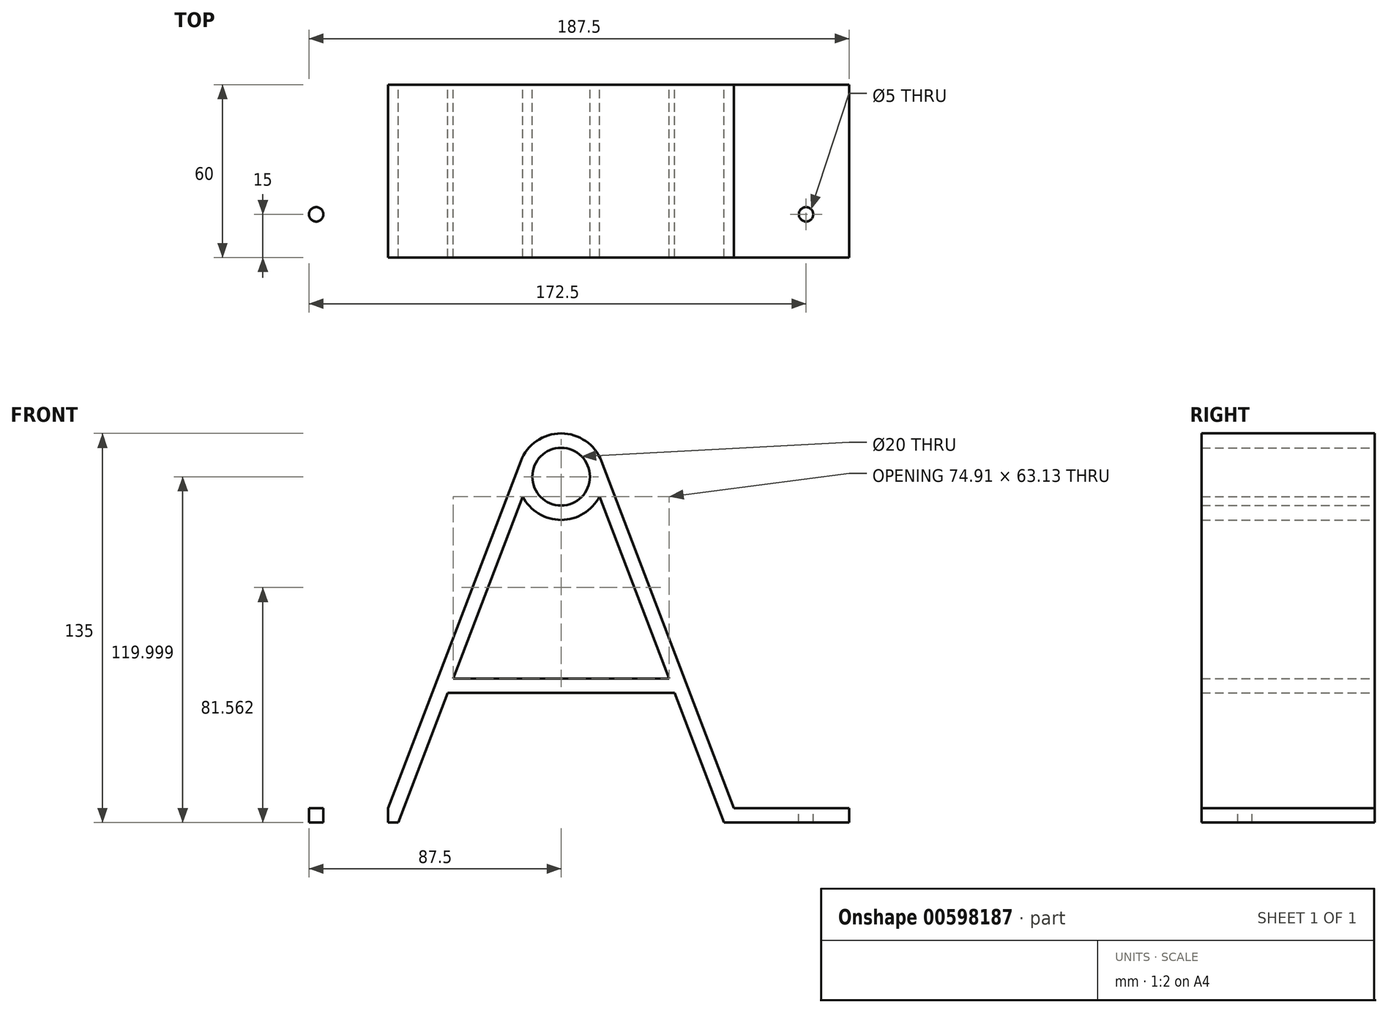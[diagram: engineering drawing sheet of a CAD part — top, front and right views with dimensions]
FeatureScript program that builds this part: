
annotation { "Feature Type Name" : "Feature", "Feature Type Description" : "" }
export const myFeature = defineFeature(function(context is Context, id is Id, definition is map)
    precondition{}
    {
        {
            var Q0;
            Q0=qCreatedBy(makeId("Front.planeOp"),FACE);
            var sketch = newSketch(context, id + "F0", { "sketchPlane" : qUnion([Q0])});
            skLineSegment(sketch, "E0", {"start": v(-100, -81.24) * mm, "end": v(-60, -81.24) * mm});
            skLineSegment(sketch, "E1", {"start": v(-60, -81.24) * mm, "end": v(-14.01, 39.11) * mm});
            skLineSegment(sketch, "E2", {"start": v(0, 109.18) * mm, "end": v(0, -148.57) * mm, "construction": true});
            skLineSegment(sketch, "E3.MirrorCS", {"start": v(60, -81.24) * mm, "end": v(14.01, 39.11) * mm});
            skLineSegment(sketch, "E4.MirrorCS", {"start": v(100, -81.24) * mm, "end": v(60, -81.24) * mm});
            skCircle(sketch, "E5", {"center": v(0, 33.76) * mm, "radius": 15 * mm});
            skCircle(sketch, "E6", {"center": v(0, 33.76) * mm, "radius": 10 * mm});
            skPoint(sketch, "E7.orphan", {"position": v(0, 75.78) * mm});
            skLineSegment(sketch, "E8", {"start": v(-100, -81.24) * mm, "end": v(-100, -86.24) * mm});
            skLineSegment(sketch, "E9", {"start": v(-100, -86.24) * mm, "end": v(100, -86.24) * mm});
            skLineSegment(sketch, "E10", {"start": v(100, -81.24) * mm, "end": v(100, -86.24) * mm});
            skLineSegment(sketch, "E11", {"start": v(-56.56, -86.24) * mm, "end": v(-13.33, 26.88) * mm});
            skLineSegment(sketch, "E12.MirrorCS", {"start": v(56.56, -86.24) * mm, "end": v(13.33, 26.88) * mm});
            skPoint(sketch, "E13.trimOffspring.end.orphan", {"position": v(-5.35, 75.78) * mm});
            skPoint(sketch, "E14.trimOffspring.end.orphan", {"position": v(5.35, 75.78) * mm});
            skPoint(sketch, "E15.orphan", {"position": v(-61.1, -98.12) * mm});
            skPoint(sketch, "E16.orphan", {"position": v(61.1, -98.12) * mm});
            skLineSegment(sketch, "E17", {"start": v(-39.36, -41.24) * mm, "end": v(39.36, -41.24) * mm});
            skLineSegment(sketch, "E18", {"start": v(-37.45, -36.24) * mm, "end": v(37.45, -36.24) * mm});
            skSolve(sketch);
        }
        {
            var Q0;
            Q0=makeQuery(id+"F0.imprint","IMPRINT",FACE,{"disambiguationData":[TD([[makeQuery(id+"F0.imprint","IMPRINT",EDGE,{"derivedFrom":sQuery(id+"F0.wireOp",EDGE,"E0")}),-1.0]])]});
            var Q1;
            {var subQ5=sQuery(id+"F0.wireOp",EDGE,"E3.MirrorCS");Q1=makeQuery(id+"F0.imprint","IMPRINT",FACE,{"disambiguationData":[TD([[makeQuery(id+"F0.imprint","IMPRINT",EDGE,{"derivedFrom":subQ5}),1.0]])]});}
            var Q2;
            Q2=makeQuery(id+"F0.imprint","IMPRINT",FACE,{"disambiguationData":[TD([[makeQuery(id+"F0.imprint","IMPRINT",EDGE,{"derivedFrom":sQuery(id+"F0.wireOp",EDGE,"E6")}),-1.0]])]});
            var Q3;
            {var subQ0=sQuery(id+"F0.wireOp",EDGE,"E17");Q3=makeQuery(id+"F0.imprint","IMPRINT",FACE,{"disambiguationData":[TD([[makeQuery(id+"F0.imprint","IMPRINT",EDGE,{"derivedFrom":subQ0}),1.0]])]});}
            extrude(context, id + "F1", {"entities" : qUnion([Q0, Q1, Q2, Q3]), "endBound" : BoundingType.SYMMETRIC, "depth" : 60 * mm, "offsetDistance" : 25 * mm});
        }
        {
            var Q0;
            Q0=makeQuery(id+"F1.opExtrude","SWEPT_FACE",FACE,{"disambiguationData":[OSD([sQuery(id+"F0.wireOp",EDGE,"E0")])]});
            var sketch = newSketch(context, id + "F2", { "sketchPlane" : qUnion([Q0])});
            skCircle(sketch, "E19", {"center": v(-85, 15) * mm, "radius": 2.5 * mm});
            skCircle(sketch, "E20.MirrorC", {"center": v(-85, -15) * mm, "radius": 2.5 * mm});
            skCircle(sketch, "E21.MirrorC", {"center": v(85, 15) * mm, "radius": 2.5 * mm});
            skCircle(sketch, "E22.MirrorC", {"center": v(85, -15) * mm, "radius": 2.5 * mm});
            skSolve(sketch);
        }
        {
            var Q0;
            Q0=makeQuery(id+"F2.imprint","IMPRINT",FACE,{"disambiguationData":[TD([[makeQuery(id+"F2.imprint","IMPRINT",EDGE,{"derivedFrom":sQuery(id+"F2.wireOp",EDGE,"E19")}),1.0]])]});
            var Q1;
            Q1=makeQuery(id+"F2.imprint","IMPRINT",FACE,{"disambiguationData":[TD([[makeQuery(id+"F2.imprint","IMPRINT",EDGE,{"derivedFrom":sQuery(id+"F2.wireOp",EDGE,"E20.MirrorC")}),-1.0]])]});
            var Q2;
            Q2=makeQuery(id+"F2.imprint","IMPRINT",FACE,{"disambiguationData":[TD([[makeQuery(id+"F2.imprint","IMPRINT",EDGE,{"derivedFrom":sQuery(id+"F2.wireOp",EDGE,"E22.MirrorC")}),1.0]])]});
            var Q3;
            Q3=makeQuery(id+"F2.imprint","IMPRINT",FACE,{"disambiguationData":[TD([[makeQuery(id+"F2.imprint","IMPRINT",EDGE,{"derivedFrom":sQuery(id+"F2.wireOp",EDGE,"E21.MirrorC")}),-1.0]])]});
            extrude(context, id + "F3", {"entities" : qUnion([Q0, Q1, Q2, Q3]), "operationType" : NewBodyOperationType.REMOVE, "endBound" : BoundingType.THROUGH_ALL, "oppositeDirection" : true, "depth" : 25 * mm, "offsetDistance" : 25 * mm});
        }
    });
